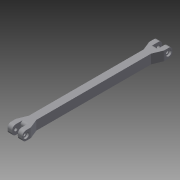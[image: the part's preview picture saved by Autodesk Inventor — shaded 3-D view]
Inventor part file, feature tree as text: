
AUTODESK INVENTOR PART (.ipt)
format: ipt  version: 2015 (Build 190159000, 159)  size: 167,936 bytes
history: native  units: mm
features: sketch x4, fillet x4, extrude x2, plane x2, mirror x2, loft x1, hole x1, other x1
ambient origin geometry x8: Origin, YZ Plane, XZ Plane, XY Plane, X Axis, Y Axis, Z Axis, Center Point
bodies: Solid1 (feature_tree)
feature tree (17):
  extrude  "Extrusion1"  Depth=10.0mm
  sketch  "Sketch2"  dims[d2=144.0mm d3=0.0mm d4=5.0mm]
  sketch  "Sketch3"  dims[d5=5.0mm d6=3.05mm d7=3.05mm d8=10.0mm]
  extrude  "Extrusion3"  Depth=5.0mm
  loft  "Loft2"
  plane  "Work Plane2"
  fillet  "Fillet4"  Radius=3.05mm
  fillet  "Fillet5"  Radius=10.0mm
  hole  "Hole1"  [1 undecoded]
  mirror  "Mirror2"
  plane  "Work Plane3"
  mirror  "Mirror3"
  fillet  "Fillet6"  [1 undecoded]
  fillet  "Fillet7"  Radius=4.0mm
  sketch  "Sketch1"  dims[d0=8.0mm d1=10.0mm]
  other  "Edges1"
  sketch  "Sketch5"  dims[d18=9.0mm d19=0.0mm d20=0.0mm d21=90.0deg d22=0.0mm d23=90.0deg d24=4.0mm d25=4.0mm d26=3.3mm d27=6.0mm d28=6.0mm d29=2.0mm d30=90.0deg d31=8.0mm d32=20.594885mm d42=3.0mm d43=3.0mm]
note: 2 required parameter values undecoded (feature->parameter linkage not recoverable at this tier; creation-order binding heuristic only, values carry confidence <= 0.55)
